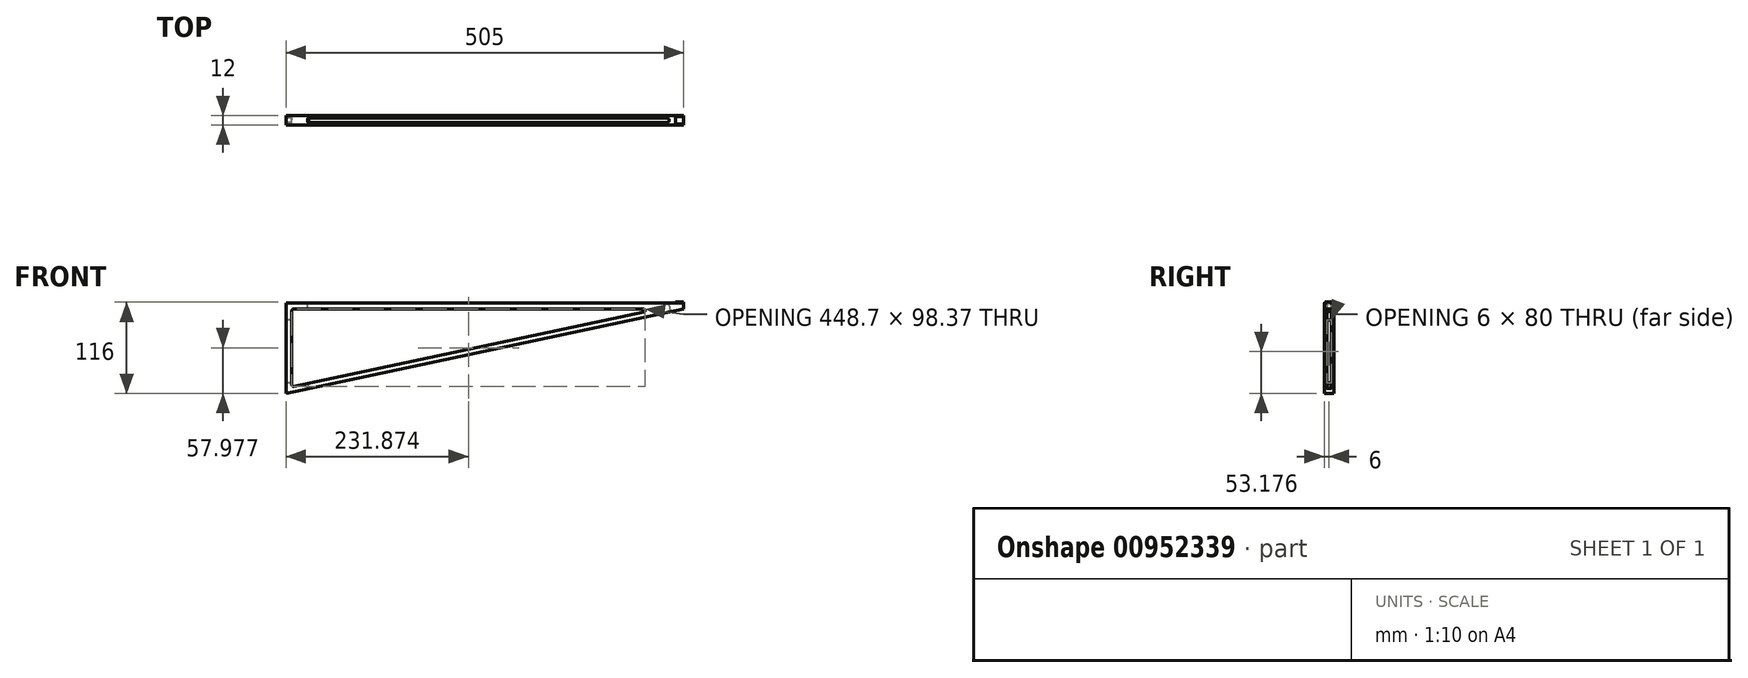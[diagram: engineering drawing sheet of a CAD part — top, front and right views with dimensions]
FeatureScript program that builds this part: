
annotation { "Feature Type Name" : "Feature", "Feature Type Description" : "" }
export const myFeature = defineFeature(function(context is Context, id is Id, definition is map)
    precondition{}
    {
        {
            var Q0;
            Q0=qCreatedBy(makeId("Front.planeOp"),FACE);
            var sketch = newSketch(context, id + "F0", { "sketchPlane" : qUnion([Q0])});
            skLineSegment(sketch, "E0.bottom", {"start": v(-222.18, 7.84) * mm, "end": v(282.82, 7.84) * mm});
            skLineSegment(sketch, "E0.top", {"start": v(-222.18, 0) * mm, "end": v(282.82, 0) * mm});
            skLineSegment(sketch, "E0.left", {"start": v(-222.18, 7.84) * mm, "end": v(-222.18, 0) * mm});
            skLineSegment(sketch, "E0.right", {"start": v(282.82, 7.84) * mm, "end": v(282.82, 0) * mm});
            skLineSegment(sketch, "E1", {"start": v(-222.18, 0) * mm, "end": v(-222.18, -107.16) * mm});
            skLineSegment(sketch, "E2", {"start": v(-222.18, -107.16) * mm, "end": v(282.82, 0) * mm});
            skLineSegment(sketch, "E3", {"start": v(-214.66, 0) * mm, "end": v(-214.66, -98.83) * mm});
            skLineSegment(sketch, "E4", {"start": v(-214.66, -98.83) * mm, "end": v(251.11, 0) * mm});
            skSolve(sketch);
        }
        {
            var Q0;
            Q0 = qSketchRegion(id + "F0", true);
            extrude(context, id + "F1", {"entities" : qUnion([Q0]), "depth" : 12 * mm, "offsetDistance" : 25 * mm});
        }
        {
            var Q0;
            Q0=makeQuery(id+"F1.opExtrude","SWEPT_EDGE",EDGE,{"disambiguationData":[OSD([sQuery(id+"F0.wireOp",EDGE,"E0.top"),sQuery(id+"F0.wireOp",EDGE,"E4")])]});
            var Q1;
            Q1=makeQuery(id+"F1.opExtrude","SWEPT_EDGE",EDGE,{"disambiguationData":[OSD([sQuery(id+"F0.wireOp",EDGE,"E0.top"),sQuery(id+"F0.wireOp",EDGE,"E3")])]});
            var Q2;
            Q2=makeQuery(id+"F1.opExtrude","SWEPT_EDGE",EDGE,{"disambiguationData":[OSD([sQuery(id+"F0.wireOp",EDGE,"E3"),sQuery(id+"F0.wireOp",EDGE,"E4")])]});
            fillet(context, id + "F2", {"entities" : qUnion([Q0, Q1, Q2]), "radius" : 2 * mm, "tangentPropagation" : true, "allowEdgeOverflow" : false});
        }
        {
            var Q0;
            Q0=makeQuery(id+"F1.opExtrude","SWEPT_FACE",FACE,{"disambiguationData":[OSD([sQuery(id+"F0.wireOp",EDGE,"E0.bottom")])]});
            var sketch = newSketch(context, id + "F3", { "sketchPlane" : qUnion([Q0])});
            skLineSegment(sketch, "E5.bottom", {"start": v(272.82, -1) * mm, "end": v(282.82, -1) * mm});
            skLineSegment(sketch, "E5.top", {"start": v(272.82, -11) * mm, "end": v(282.82, -11) * mm});
            skLineSegment(sketch, "E5.left", {"start": v(272.82, -1) * mm, "end": v(272.82, -11) * mm});
            skLineSegment(sketch, "E5.right", {"start": v(282.82, -1) * mm, "end": v(282.82, -11) * mm});
            skSolve(sketch);
        }
        {
            var Q0;
            Q0=makeQuery(id+"F3.imprint","IMPRINT",FACE,{"disambiguationData":[TD([[makeQuery(id+"F3.imprint","IMPRINT",EDGE,{"derivedFrom":sQuery(id+"F3.wireOp",EDGE,"E5.bottom")}),-1.0]])]});
            extrude(context, id + "F4", {"entities" : qUnion([Q0]), "operationType" : NewBodyOperationType.ADD, "depth" : 1 * mm, "offsetDistance" : 25 * mm});
        }
        {
            var Q0;
            Q0=makeQuery(id+"F1.opExtrude","SWEPT_FACE",FACE,{"disambiguationData":[OSD([sQuery(id+"F0.wireOp",EDGE,"E0.bottom")])]});
            var sketch = newSketch(context, id + "F5", { "sketchPlane" : qUnion([Q0])});
            skLineSegment(sketch, "E6.bottom", {"start": v(-194.8, -3) * mm, "end": v(260.2, -3) * mm});
            skLineSegment(sketch, "E6.top", {"start": v(-194.8, -9) * mm, "end": v(260.2, -9) * mm});
            skLineSegment(sketch, "E6.left", {"start": v(-194.8, -3) * mm, "end": v(-194.8, -9) * mm});
            skLineSegment(sketch, "E6.right", {"start": v(260.2, -3) * mm, "end": v(260.2, -9) * mm});
            skSolve(sketch);
        }
        {
            var Q0;
            Q0=makeQuery(id+"F5.imprint","IMPRINT",FACE,{"disambiguationData":[TD([[makeQuery(id+"F5.imprint","IMPRINT",EDGE,{"derivedFrom":sQuery(id+"F5.wireOp",EDGE,"E6.bottom")}),-1.0]])]});
            extrude(context, id + "F6", {"entities" : qUnion([Q0]), "operationType" : NewBodyOperationType.REMOVE, "oppositeDirection" : true, "depth" : 12 * mm, "offsetDistance" : 25 * mm});
        }
        {
            var Q0;
            Q0=makeQuery(id+"F1.opExtrude","SWEPT_FACE",FACE,{"disambiguationData":[OSD([sQuery(id+"F0.wireOp",EDGE,"E2")])]});
            var sketch = newSketch(context, id + "F7", { "sketchPlane" : qUnion([Q0])});
            skLineSegment(sketch, "E7.bottom", {"start": v(-210.38, 9) * mm, "end": v(259.62, 9) * mm});
            skLineSegment(sketch, "E7.top", {"start": v(-210.38, 3) * mm, "end": v(259.62, 3) * mm});
            skLineSegment(sketch, "E7.left", {"start": v(-210.38, 9) * mm, "end": v(-210.38, 3) * mm});
            skLineSegment(sketch, "E7.right", {"start": v(259.62, 9) * mm, "end": v(259.62, 3) * mm});
            skSolve(sketch);
        }
        {
            var Q0;
            Q0=makeQuery(id+"F7.imprint","IMPRINT",FACE,{"disambiguationData":[TD([[makeQuery(id+"F7.imprint","IMPRINT",EDGE,{"derivedFrom":sQuery(id+"F7.wireOp",EDGE,"E7.bottom")}),-1.0]])]});
            extrude(context, id + "F8", {"entities" : qUnion([Q0]), "operationType" : NewBodyOperationType.REMOVE, "oppositeDirection" : true, "depth" : 25 * mm, "offsetDistance" : 25 * mm});
        }
        {
            var Q0;
            Q0=makeQuery(id+"F1.opExtrude","SWEPT_FACE",FACE,{"disambiguationData":[OSD([sQuery(id+"F0.wireOp",EDGE,"E0.left"),sQuery(id+"F0.wireOp",EDGE,"E1")])]});
            var sketch = newSketch(context, id + "F9", { "sketchPlane" : qUnion([Q0])});
            skLineSegment(sketch, "E8.bottom", {"start": v(3, -13.98) * mm, "end": v(9, -13.98) * mm});
            skLineSegment(sketch, "E8.top", {"start": v(3, -93.98) * mm, "end": v(9, -93.98) * mm});
            skLineSegment(sketch, "E8.left", {"start": v(3, -13.98) * mm, "end": v(3, -93.98) * mm});
            skLineSegment(sketch, "E8.right", {"start": v(9, -13.98) * mm, "end": v(9, -93.98) * mm});
            skSolve(sketch);
        }
        {
            var Q0;
            Q0=makeQuery(id+"F9.imprint","IMPRINT",FACE,{"disambiguationData":[TD([[makeQuery(id+"F9.imprint","IMPRINT",EDGE,{"derivedFrom":sQuery(id+"F9.wireOp",EDGE,"E8.bottom")}),-1.0]])]});
            extrude(context, id + "F10", {"entities" : qUnion([Q0]), "operationType" : NewBodyOperationType.REMOVE, "oppositeDirection" : true, "depth" : 13 * mm, "offsetDistance" : 25 * mm});
        }
        {
            var Q0;
            Q0=makeQuery(id+"F8.boolean.opBoolean","COPY",EDGE,{"derivedFrom":makeQuery(id+"F8.opExtrude","SWEPT_EDGE",EDGE,{"disambiguationData":[OSD([sQuery(id+"F7.wireOp",EDGE,"E7.bottom"),sQuery(id+"F7.wireOp",EDGE,"E7.right")])]})});
            var Q1;
            Q1=makeQuery(id+"F8.boolean.opBoolean","COPY",EDGE,{"derivedFrom":makeQuery(id+"F8.opExtrude","SWEPT_EDGE",EDGE,{"disambiguationData":[OSD([sQuery(id+"F7.wireOp",EDGE,"E7.bottom"),sQuery(id+"F7.wireOp",EDGE,"E7.left")])]})});
            var Q2;
            Q2=makeQuery(id+"F8.boolean.opBoolean","COPY",EDGE,{"derivedFrom":makeQuery(id+"F8.opExtrude","SWEPT_EDGE",EDGE,{"disambiguationData":[OSD([sQuery(id+"F7.wireOp",EDGE,"E7.top"),sQuery(id+"F7.wireOp",EDGE,"E7.left")])]})});
            var Q3;
            Q3=makeQuery(id+"F6.boolean.opBoolean","COPY",EDGE,{"derivedFrom":makeQuery(id+"F6.opExtrude","SWEPT_EDGE",EDGE,{"disambiguationData":[OSD([sQuery(id+"F5.wireOp",EDGE,"E6.top"),sQuery(id+"F5.wireOp",EDGE,"E6.left")])]})});
            var Q4;
            Q4=makeQuery(id+"F6.boolean.opBoolean","COPY",EDGE,{"derivedFrom":makeQuery(id+"F6.opExtrude","SWEPT_EDGE",EDGE,{"disambiguationData":[OSD([sQuery(id+"F5.wireOp",EDGE,"E6.bottom"),sQuery(id+"F5.wireOp",EDGE,"E6.left")])]})});
            var Q5;
            Q5=makeQuery(id+"F10.boolean.opBoolean","COPY",EDGE,{"derivedFrom":makeQuery(id+"F10.opExtrude","SWEPT_EDGE",EDGE,{"disambiguationData":[OSD([sQuery(id+"F9.wireOp",EDGE,"E8.bottom"),sQuery(id+"F9.wireOp",EDGE,"E8.left")])]})});
            var Q6;
            Q6=makeQuery(id+"F10.boolean.opBoolean","COPY",EDGE,{"derivedFrom":makeQuery(id+"F10.opExtrude","SWEPT_EDGE",EDGE,{"disambiguationData":[OSD([sQuery(id+"F9.wireOp",EDGE,"E8.bottom"),sQuery(id+"F9.wireOp",EDGE,"E8.right")])]})});
            var Q7;
            Q7=makeQuery(id+"F10.boolean.opBoolean","COPY",EDGE,{"derivedFrom":makeQuery(id+"F10.opExtrude","SWEPT_EDGE",EDGE,{"disambiguationData":[OSD([sQuery(id+"F9.wireOp",EDGE,"E8.top"),sQuery(id+"F9.wireOp",EDGE,"E8.left")])]})});
            var Q8;
            Q8=makeQuery(id+"F10.boolean.opBoolean","COPY",EDGE,{"derivedFrom":makeQuery(id+"F10.opExtrude","SWEPT_EDGE",EDGE,{"disambiguationData":[OSD([sQuery(id+"F9.wireOp",EDGE,"E8.top"),sQuery(id+"F9.wireOp",EDGE,"E8.right")])]})});
            var Q9;
            Q9=makeQuery(id+"F8.boolean.opBoolean","COPY",EDGE,{"derivedFrom":makeQuery(id+"F8.opExtrude","SWEPT_EDGE",EDGE,{"disambiguationData":[OSD([sQuery(id+"F7.wireOp",EDGE,"E7.top"),sQuery(id+"F7.wireOp",EDGE,"E7.right")])]})});
            var Q10;
            Q10=makeQuery(id+"F8.boolean.opBoolean","COPY",FACE,{"derivedFrom":makeQuery(id+"F8.opExtrude","SWEPT_FACE",FACE,{"disambiguationData":[OSD([sQuery(id+"F7.wireOp",EDGE,"E7.right")])]})});
            fillet(context, id + "F11", {"entities" : qUnion([Q0, Q1, Q2, Q3, Q4, Q5, Q6, Q7, Q8, Q9, Q10]), "radius" : 2 * mm, "tangentPropagation" : true, "allowEdgeOverflow" : false});
        }
    });
